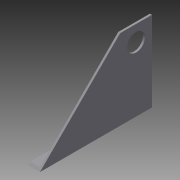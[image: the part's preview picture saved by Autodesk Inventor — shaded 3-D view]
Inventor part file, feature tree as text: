
AUTODESK INVENTOR PART (.ipt)
format: ipt  version: 2013 (Build 170138000, 138)  size: 91,648 bytes
history: native  units: in
note: dims shown in document units (in); Inventor stores cm internally (conversion verified against a paired STEP export)
features: extrude x2, sketch x2
ambient origin geometry x8: Origin, YZ Plane, XZ Plane, XY Plane, X Axis, Y Axis, Z Axis, Center Point
bodies: Solid1 (feature_tree)
feature tree (4):
  extrude  "Extrusion1"  TaperAngle=0.0deg  [1 undecoded]
  extrude  "Extrusion2"  Depth=1.0in
  sketch  "Sketch1"  dims[d0=4.063in d1=0.0in]
  sketch  "Sketch2"  dims[d2=1.125in d3=1.0in d4=0.0in d5=1.0in d6=90.0deg d7=1.0in d8=90.0deg d9=135.0deg d10=0.125in d11=0.0in d12=0.125in d13=90.0deg d14=0.625in d15=0.0in]
note: 1 required parameter value undecoded (feature->parameter linkage not recoverable at this tier; creation-order binding heuristic only, values carry confidence <= 0.55)
